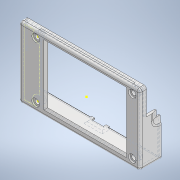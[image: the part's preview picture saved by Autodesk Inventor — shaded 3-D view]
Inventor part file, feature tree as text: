
AUTODESK INVENTOR PART (.ipt)
format: ipt  version: 2021 (Build 250183000, 183)  size: 324,096 bytes
history: native  units: mm
features: other x7, fillet x4, plane x3, sketch x1, projected_geometry x1
ambient origin geometry x8: Origin, YZ Plane, XZ Plane, XY Plane, X Axis, Y Axis, Z Axis, Center Point
bodies: Solid1 (feature_tree)
feature tree (16):
  other  "improved_case.ipt"
  plane  "Work Plane1"
  plane  "Work Plane2"
  plane  "Work Plane3"
  other  "Lip1"
  fillet  "Fillet1"  Radius=10.0mm
  other  "Lip2"
  fillet  "Fillet2"  Radius=0.9mm
  other  "Lip3"
  fillet  "Fillet3"  Radius=0.9mm
  other  "Lip4"
  sketch  "Sketch1"  dims[d1=1.1mm d2=0.9mm d3=0.0mm d4=0.0mm d5=0.0mm d6=0.0mm d7=0.9mm d8=1.1mm d9=0.9mm d10=0.0mm d11=0.0mm d12=0.0mm d13=0.0mm d14=0.9mm d15=1.1mm d16=0.9mm d17=0.0mm d18=0.0mm d19=0.0mm d20=0.0mm d21=0.9mm d22=1.1mm d23=0.9mm d24=0.0mm d25=0.0mm d26=0.0mm d27=0.0mm d28=0.9mm]
  fillet  "Fillet4"  Radius=0.9mm
  other  "Solid3::improved_case.ipt"
  other  "TaggingFeature1"
  projected_geometry  "Projected Loop1"
